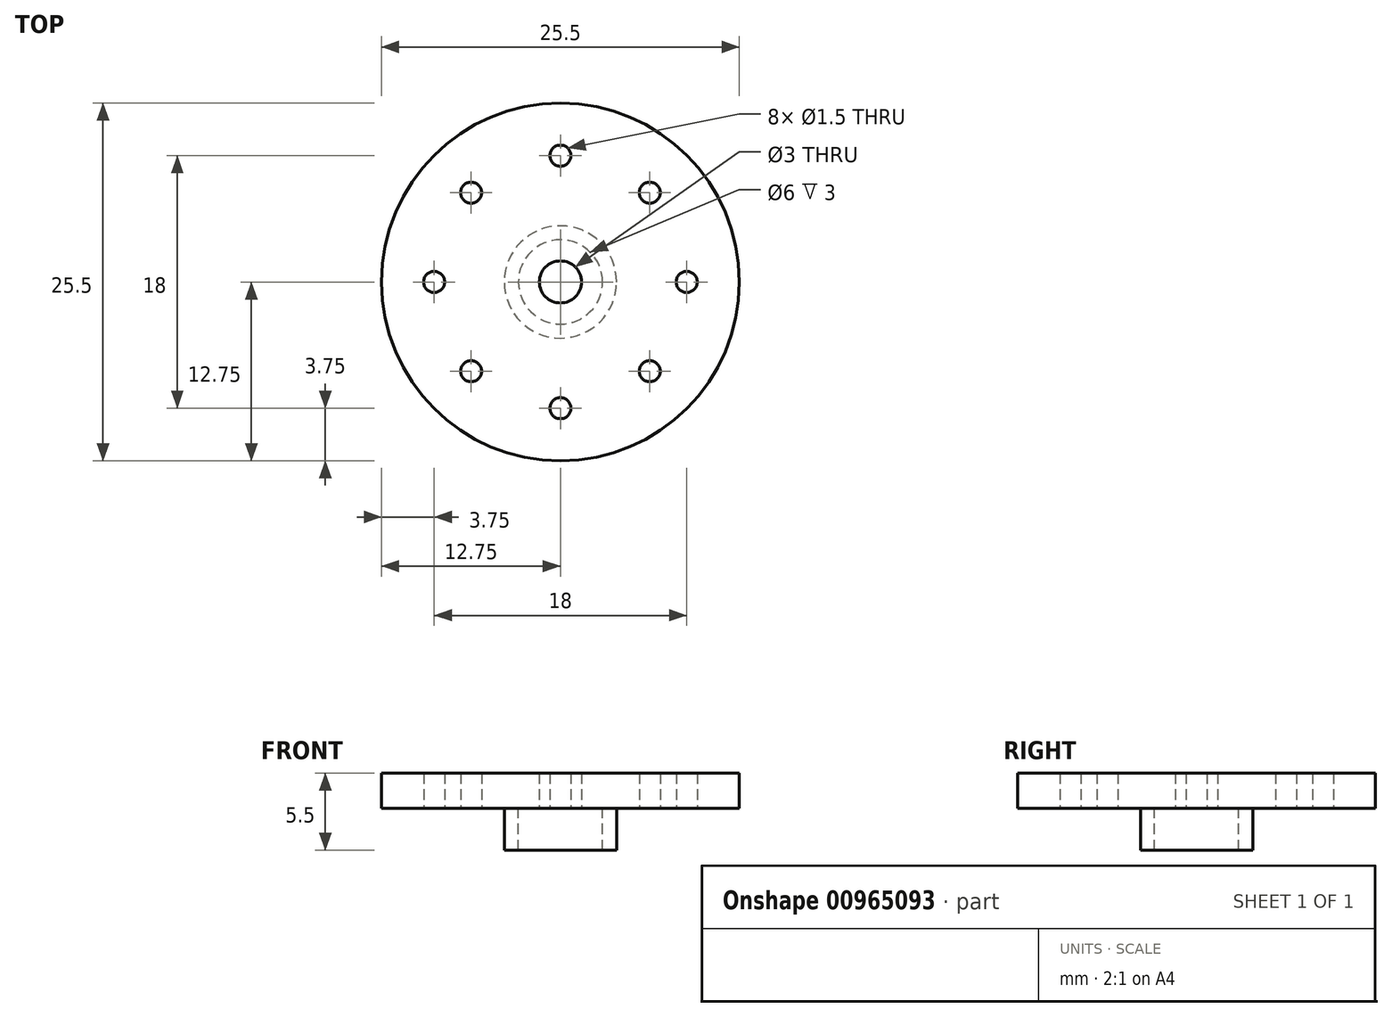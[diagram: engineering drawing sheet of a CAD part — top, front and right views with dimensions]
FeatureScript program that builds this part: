
annotation { "Feature Type Name" : "Feature", "Feature Type Description" : "" }
export const myFeature = defineFeature(function(context is Context, id is Id, definition is map)
    precondition{}
    {
        {
            var Q0;
            Q0=qCreatedBy(makeId("Top.planeOp"),FACE);
            var sketch = newSketch(context, id + "F0", { "sketchPlane" : qUnion([Q0])});
            skCircle(sketch, "E0", {"center": v(0, 0) * mm, "radius": 12.75 * mm});
            skLineSegment(sketch, "E1", {"start": v(-10, -10) * mm, "end": v(10, 10) * mm, "construction": true});
            skLineSegment(sketch, "E2", {"start": v(-10, 10) * mm, "end": v(10, -10) * mm, "construction": true});
            skCircle(sketch, "E3", {"center": v(0, 9) * mm, "radius": 0.75 * mm});
            skCircle(sketch, "E4", {"center": v(6.36, 6.36) * mm, "radius": 0.75 * mm});
            skCircle(sketch, "E5", {"center": v(9, 0) * mm, "radius": 0.75 * mm});
            skCircle(sketch, "E6", {"center": v(6.36, -6.36) * mm, "radius": 0.75 * mm});
            skCircle(sketch, "E7", {"center": v(0, -9) * mm, "radius": 0.75 * mm});
            skCircle(sketch, "E8", {"center": v(-6.36, -6.36) * mm, "radius": 0.75 * mm});
            skCircle(sketch, "E9", {"center": v(-9, 0) * mm, "radius": 0.75 * mm});
            skCircle(sketch, "E10", {"center": v(-6.36, 6.36) * mm, "radius": 0.75 * mm});
            skCircle(sketch, "E11", {"center": v(0, 0) * mm, "radius": 3 * mm});
            skCircle(sketch, "E12", {"center": v(0, 0) * mm, "radius": 4 * mm});
            skCircle(sketch, "E13", {"center": v(0, 0) * mm, "radius": 1.5 * mm});
            skSolve(sketch);
        }
        {
            var Q0;
            Q0=makeQuery(id+"F0.imprint","IMPRINT",FACE,{"disambiguationData":[TD([[makeQuery(id+"F0.imprint","IMPRINT",EDGE,{"derivedFrom":sQuery(id+"F0.wireOp",EDGE,"E0")}),1.0]])]});
            var Q1;
            Q1=makeQuery(id+"F0.imprint","IMPRINT",FACE,{"disambiguationData":[TD([[makeQuery(id+"F0.imprint","IMPRINT",EDGE,{"derivedFrom":sQuery(id+"F0.wireOp",EDGE,"E11")}),1.0]])]});
            var Q2;
            Q2=makeQuery(id+"F0.imprint","IMPRINT",FACE,{"disambiguationData":[TD([[makeQuery(id+"F0.imprint","IMPRINT",EDGE,{"derivedFrom":sQuery(id+"F0.wireOp",EDGE,"E11")}),-1.0]])]});
            extrude(context, id + "F1", {"entities" : qUnion([Q0, Q1, Q2]), "depth" : 2.5 * mm, "offsetDistance" : 25 * mm});
        }
        {
            var Q0;
            Q0=makeQuery(id+"F0.imprint","IMPRINT",FACE,{"disambiguationData":[TD([[makeQuery(id+"F0.imprint","IMPRINT",EDGE,{"derivedFrom":sQuery(id+"F0.wireOp",EDGE,"E11")}),-1.0]])]});
            extrude(context, id + "F2", {"entities" : qUnion([Q0]), "operationType" : NewBodyOperationType.ADD, "oppositeDirection" : true, "depth" : 3 * mm, "offsetDistance" : 25 * mm});
        }
    });
